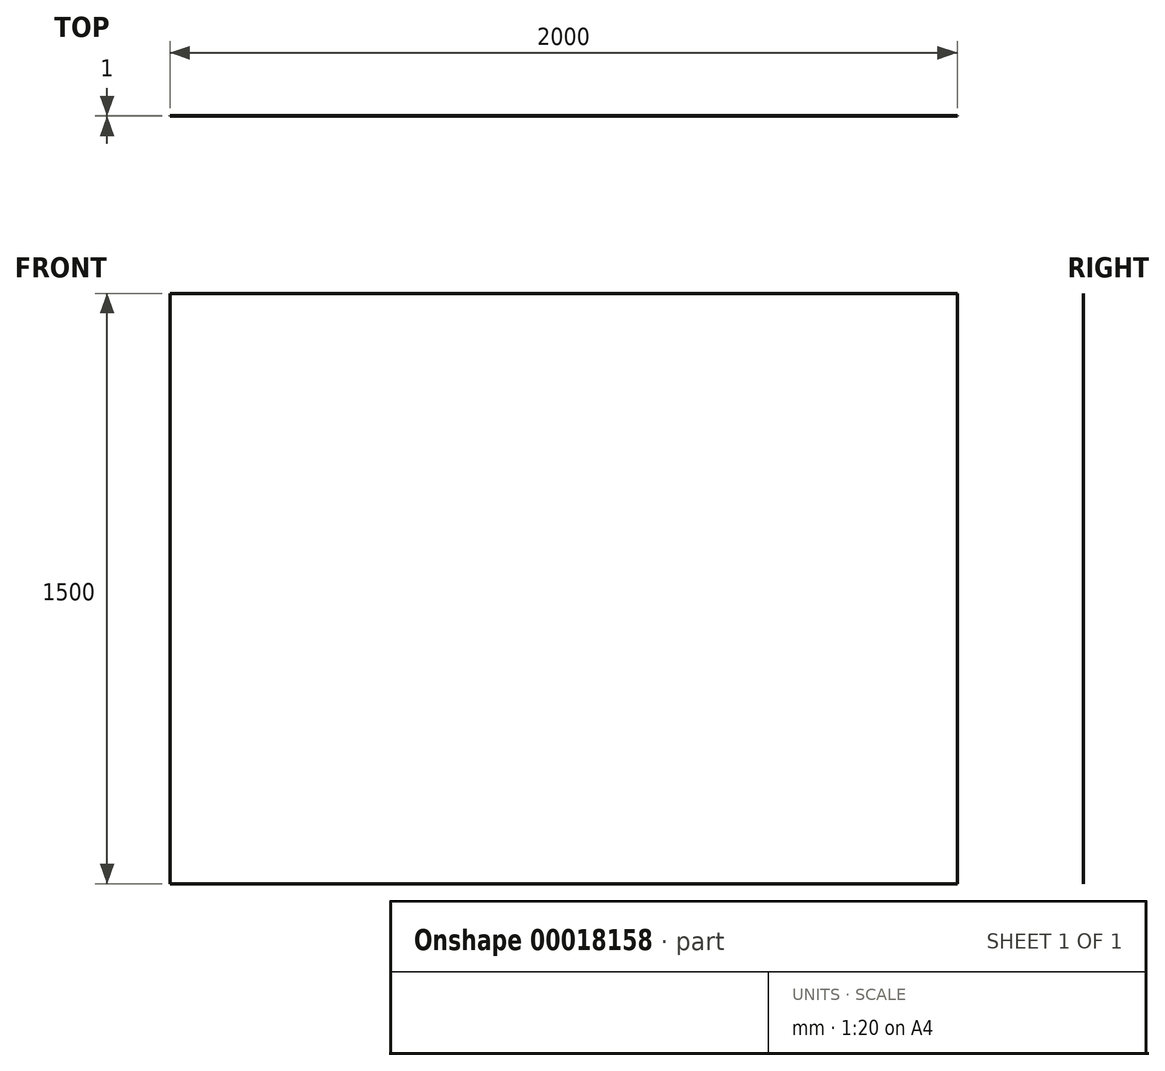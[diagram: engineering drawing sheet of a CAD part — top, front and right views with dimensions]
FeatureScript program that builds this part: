
annotation { "Feature Type Name" : "Feature", "Feature Type Description" : "" }
export const myFeature = defineFeature(function(context is Context, id is Id, definition is map)
    precondition{}
    {
        {
            var Q0;
            Q0=qCreatedBy(makeId("Front.planeOp"),FACE);
            var sketch = newSketch(context, id + "F0", { "sketchPlane" : qUnion([Q0])});
            skLineSegment(sketch, "E0.bottom", {"start": v(-997.8, 688.35) * mm, "end": v(1002.2, 688.35) * mm});
            skLineSegment(sketch, "E0.top", {"start": v(-997.8, -811.65) * mm, "end": v(1002.2, -811.65) * mm});
            skLineSegment(sketch, "E0.left", {"start": v(-997.8, 688.35) * mm, "end": v(-997.8, -811.65) * mm});
            skLineSegment(sketch, "E0.right", {"start": v(1002.2, 688.35) * mm, "end": v(1002.2, -811.65) * mm});
            skSolve(sketch);
        }
        {
            var Q0;
            Q0 = qSketchRegion(id + "F0", true);
            extrude(context, id + "F1", {"entities" : qUnion([Q0]), "depth" : 1 * mm});
        }
    });
